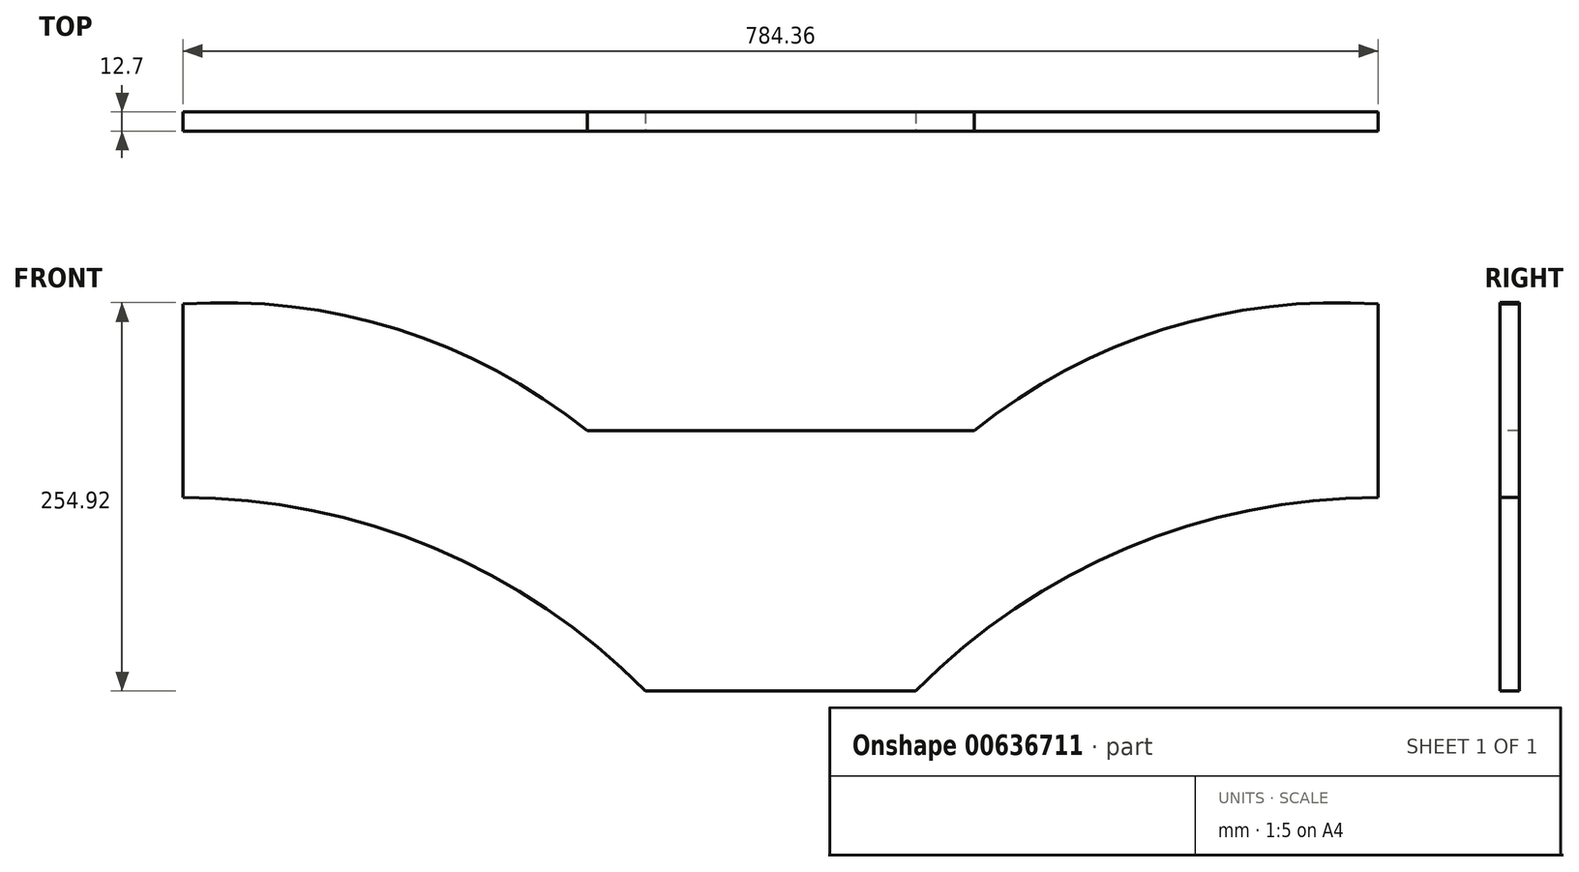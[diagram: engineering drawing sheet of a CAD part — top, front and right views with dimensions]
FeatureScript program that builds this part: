
annotation { "Feature Type Name" : "Feature", "Feature Type Description" : "" }
export const myFeature = defineFeature(function(context is Context, id is Id, definition is map)
    precondition{}
    {
        {
            var Q0;
            Q0=qCreatedBy(makeId("Front.planeOp"),FACE);
            var sketch = newSketch(context, id + "F0", { "sketchPlane" : qUnion([Q0])});
            skArc(sketch, "E0", {"start": v(-153.48, -3.64) * mm, "mid": v(-292.38, 90.33) * mm, "end": v(-456.8, 123.36) * mm, "construction": true});
            skArc(sketch, "E1", {"start": v(-153.48, -3.64) * mm, "mid": v(-292.38, 90.33) * mm, "end": v(-456.8, 123.36) * mm});
            skLineSegment(sketch, "E2", {"start": v(-456.8, 123.36) * mm, "end": v(-456.8, 250.36) * mm});
            skArc(sketch, "E3", {"start": v(-191.62, 167.2) * mm, "mid": v(-316.35, 233.82) * mm, "end": v(-456.8, 250.36) * mm});
            skArc(sketch, "E4.MirrorCS", {"start": v(24.24, -3.64) * mm, "mid": v(163.15, 90.33) * mm, "end": v(327.56, 123.36) * mm});
            skLineSegment(sketch, "E5.MirrorCS", {"start": v(327.56, 123.36) * mm, "end": v(327.56, 250.36) * mm});
            skArc(sketch, "E6.MirrorCS", {"start": v(62.38, 167.2) * mm, "mid": v(187.12, 233.82) * mm, "end": v(327.56, 250.36) * mm});
            skLineSegment(sketch, "E7", {"start": v(-191.62, 167.2) * mm, "end": v(62.38, 167.2) * mm});
            skLineSegment(sketch, "E8", {"start": v(-153.48, -3.64) * mm, "end": v(24.24, -3.64) * mm});
            skSolve(sketch);
        }
        {
            var Q0;
            Q0 = qSketchRegion(id + "F0", true);
            extrude(context, id + "F1", {"entities" : qUnion([Q0]), "oppositeDirection" : true, "depth" : 12.7 * mm, "offsetDistance" : 25.4 * mm});
        }
    });
